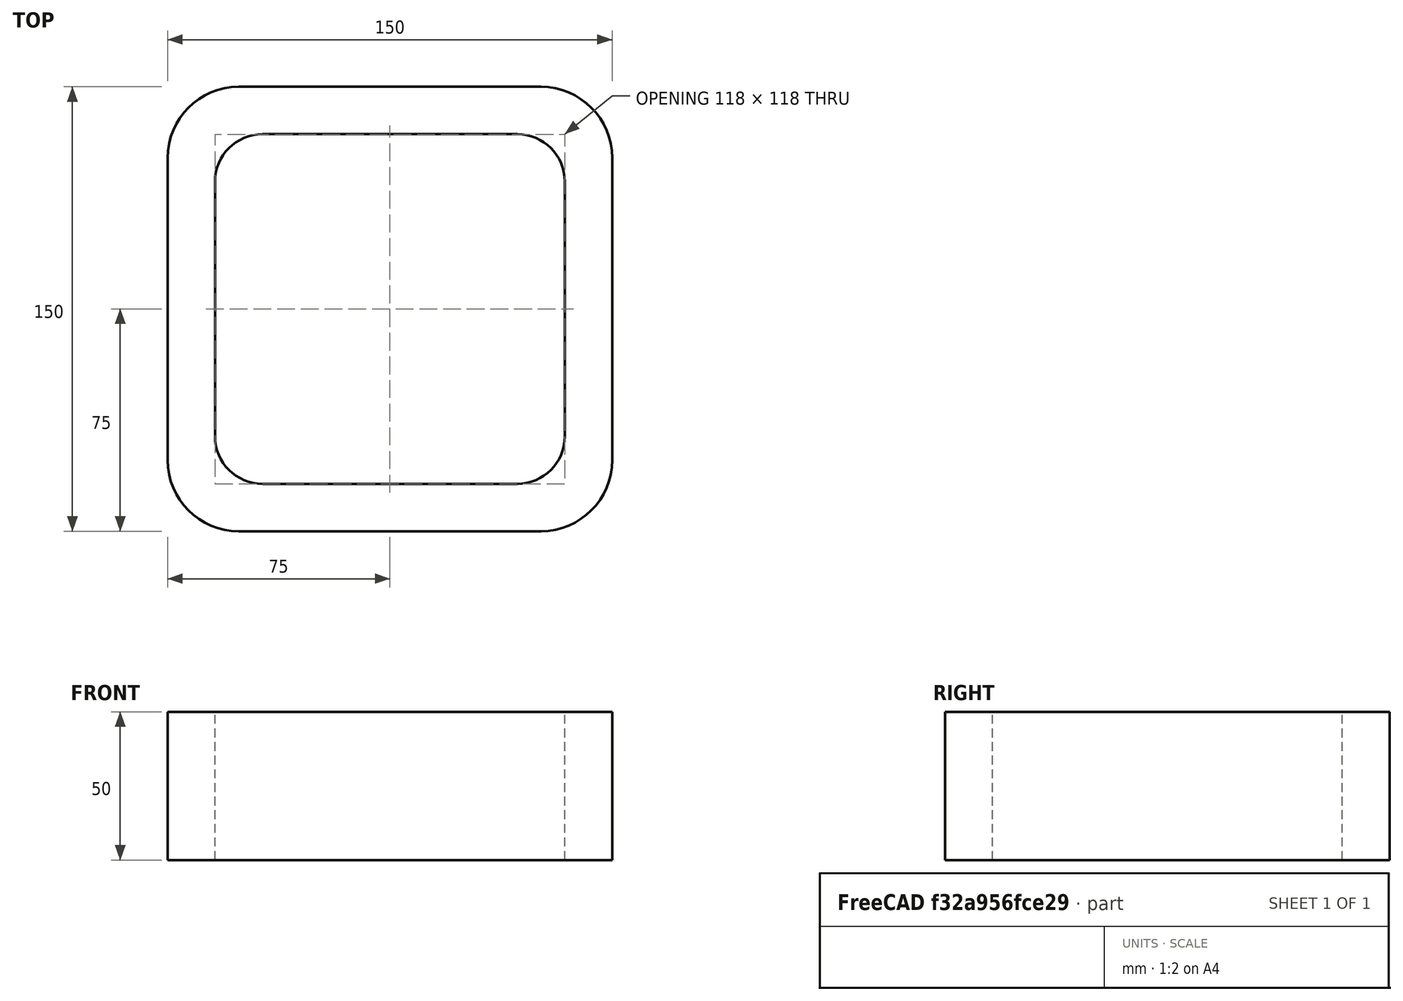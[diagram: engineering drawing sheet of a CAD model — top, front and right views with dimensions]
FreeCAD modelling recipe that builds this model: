
FCSTD DOCUMENT  (FreeCAD 0.15R4671 (Git))
Label: Square hollow section 150x150x16 EN10219 S235JRH
License: All rights reserved
LicenseURL: http://en.wikipedia.org/wiki/All_rights_reserved
objects: Sketcher::SketchObject×1, Part::Extrusion×1
note: 2 computed .brp shape members not serialized (recipe doc carries the construction recipe); baked Part::Feature solids carry a one-line shape summary decoded from their .brp

FEATURE [Sketcher::SketchObject] Sketch
  sketch-geometry (16):
    g0: LineSegment StartX=-43 StartY=59 StartZ=0 EndX=43 EndY=59 EndZ=0
    g1: LineSegment StartX=59 StartY=43 StartZ=0 EndX=59 EndY=-43 EndZ=0
    g2: LineSegment StartX=43 StartY=-59 StartZ=0 EndX=-43 EndY=-59 EndZ=0
    g3: LineSegment StartX=-59 StartY=-43 StartZ=0 EndX=-59 EndY=43 EndZ=0
    g4: LineSegment StartX=-51 StartY=75 StartZ=0 EndX=51 EndY=75 EndZ=0
    g5: LineSegment StartX=75 StartY=51 StartZ=0 EndX=75 EndY=-51 EndZ=0
    g6: LineSegment StartX=51 StartY=-75 StartZ=0 EndX=-51 EndY=-75 EndZ=0
    g7: LineSegment StartX=-75 StartY=-51 StartZ=0 EndX=-75 EndY=51 EndZ=0
    g8: ArcOfCircle CenterX=-43 CenterY=43 CenterZ=0 NormalX=0 NormalY=0 NormalZ=1 Radius=16 StartAngle=1.5708 EndAngle=3.14159
    g9: ArcOfCircle CenterX=43 CenterY=43 CenterZ=0 NormalX=0 NormalY=0 NormalZ=1 Radius=16 StartAngle=0 EndAngle=1.5708
    g10: ArcOfCircle CenterX=43 CenterY=-43 CenterZ=0 NormalX=0 NormalY=0 NormalZ=1 Radius=16 StartAngle=4.71239 EndAngle=6.28319
    g11: ArcOfCircle CenterX=-43 CenterY=-43 CenterZ=0 NormalX=0 NormalY=0 NormalZ=1 Radius=16 StartAngle=3.14159 EndAngle=4.71239
    g12: ArcOfCircle CenterX=51 CenterY=51 CenterZ=0 NormalX=0 NormalY=0 NormalZ=1 Radius=24 StartAngle=0 EndAngle=1.5708
    g13: ArcOfCircle CenterX=51 CenterY=-51 CenterZ=0 NormalX=0 NormalY=0 NormalZ=1 Radius=24 StartAngle=4.71239 EndAngle=6.28319
    g14: ArcOfCircle CenterX=-51 CenterY=-51 CenterZ=0 NormalX=0 NormalY=0 NormalZ=1 Radius=24 StartAngle=3.14159 EndAngle=4.71239
    g15: ArcOfCircle CenterX=-51 CenterY=51 CenterZ=0 NormalX=0 NormalY=0 NormalZ=1 Radius=24 StartAngle=1.5708 EndAngle=3.14159
  constraints (36):
    c: Horizontal(g2)
    c: Vertical(g3)
    c: Horizontal(g6)
    c: Vertical(g7)
    c: Tangent(g3,g8) = 1.5708
    c: Tangent(g0,g8) = 1.5708
    c: Tangent(g0,g9) = 1.5708
    c: Tangent(g1,g9) = 1.5708
    c: Tangent(g1,g10) = 1.5708
    c: Tangent(g2,g10) = 1.5708
    c: Tangent(g2,g11) = 1.5708
    c: Tangent(g3,g11) = 1.5708
    c: Tangent(g4,g12) = 1.5708
    c: Tangent(g5,g12) = 1.5708
    c: Tangent(g5,g13) = 1.5708
    c: Tangent(g6,g13) = 1.5708
    c: Tangent(g6,g14) = 1.5708
    c: Tangent(g7,g14) = 1.5708
    c: Tangent(g7,g15) = 1.5708
    c: Tangent(g4,g15) = 1.5708
    c: Equal(g9,g8)
    c: Equal(g9,g11)
    c: Equal(g9,g10)
    c: Equal(g12,g15)
    c: Equal(g12,g14)
    c: Equal(g12,g13)
    c: Symmetric(g4,g6,g-1)
    c: Symmetric(g7,g5,g-2)
    c: DistanceY(g4,g6) = -150
    c: DistanceX(g7,g5) = 150
    c: Symmetric(g3,g1,g-2)
    c: Symmetric(g0,g2,g-1)
    c: DistanceY(g0,g4) = 16
    c: DistanceX(g5,g1) = -16
    c: Radius(g9) = 16
    c: Radius(g12) = 24
FEATURE [Part::Extrusion] Extrude  label="Square hollow section 150x150x16 EN10219 S235JRH"
  Base = -> Sketch
  Dir = (0,0,50)
  Solid = true
